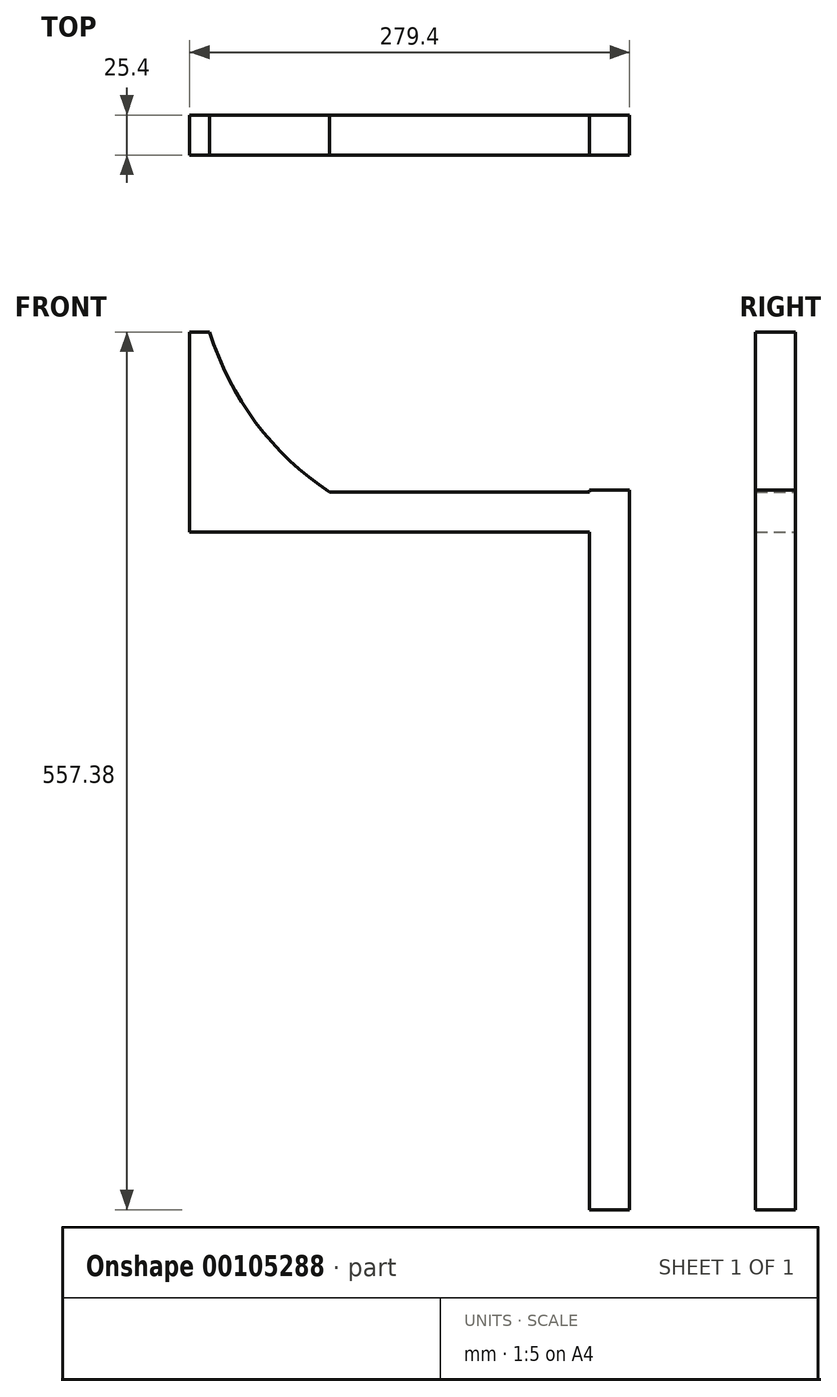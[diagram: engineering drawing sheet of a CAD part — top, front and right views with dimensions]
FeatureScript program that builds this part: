
annotation { "Feature Type Name" : "Feature", "Feature Type Description" : "" }
export const myFeature = defineFeature(function(context is Context, id is Id, definition is map)
    precondition{}
    {
        {
            var Q0;
            Q0=qCreatedBy(makeId("Top.planeOp"),FACE);
            var sketch = newSketch(context, id + "F0", { "sketchPlane" : qUnion([Q0])});
            skLineSegment(sketch, "E0.bottom", {"start": v(0, 0) * mm, "end": v(25.4, 0) * mm});
            skLineSegment(sketch, "E0.top", {"start": v(0, -25.4) * mm, "end": v(25.4, -25.4) * mm});
            skLineSegment(sketch, "E0.left", {"start": v(0, 0) * mm, "end": v(0, -25.4) * mm});
            skLineSegment(sketch, "E0.right", {"start": v(25.4, 0) * mm, "end": v(25.4, -25.4) * mm});
            skSolve(sketch);
        }
        {
            var Q0;
            Q0=makeQuery(id+"F0.imprint","IMPRINT",FACE,{"disambiguationData":[TD([[makeQuery(id+"F0.imprint","IMPRINT",EDGE,{"derivedFrom":sQuery(id+"F0.wireOp",EDGE,"E0.bottom")}),-1.0]])]});
            extrude(context, id + "F1", {"entities" : qUnion([Q0]), "depth" : 457.2 * mm});
        }
        {
            var Q0;
            Q0=qCreatedBy(makeId("Front.planeOp"),FACE);
            var sketch = newSketch(context, id + "F2", { "sketchPlane" : qUnion([Q0])});
            skLineSegment(sketch, "E1", {"start": v(0, 455.78) * mm, "end": v(0, 430.38) * mm});
            skLineSegment(sketch, "E2", {"start": v(0, 430.38) * mm, "end": v(-254, 430.38) * mm});
            skLineSegment(sketch, "E3", {"start": v(-254, 430.38) * mm, "end": v(-254, 557.38) * mm});
            skLineSegment(sketch, "E4", {"start": v(-254, 557.38) * mm, "end": v(-241.3, 557.38) * mm});
            skLineSegment(sketch, "E5", {"start": v(0, 455.78) * mm, "end": v(-165.1, 455.78) * mm});
            skArc(sketch, "E6", {"start": v(-241.3, 557.38) * mm, "mid": v(-212.1, 499.9) * mm, "end": v(-165.1, 455.78) * mm});
            skSolve(sketch);
        }
        {
            var Q0;
            Q0=makeQuery(id+"F2.imprint","IMPRINT",FACE,{"disambiguationData":[TD([[makeQuery(id+"F2.imprint","IMPRINT",EDGE,{"derivedFrom":sQuery(id+"F2.wireOp",EDGE,"E1")}),-1.0]])]});
            extrude(context, id + "F3", {"entities" : qUnion([Q0]), "operationType" : NewBodyOperationType.ADD, "depth" : 25.4 * mm});
        }
    });
